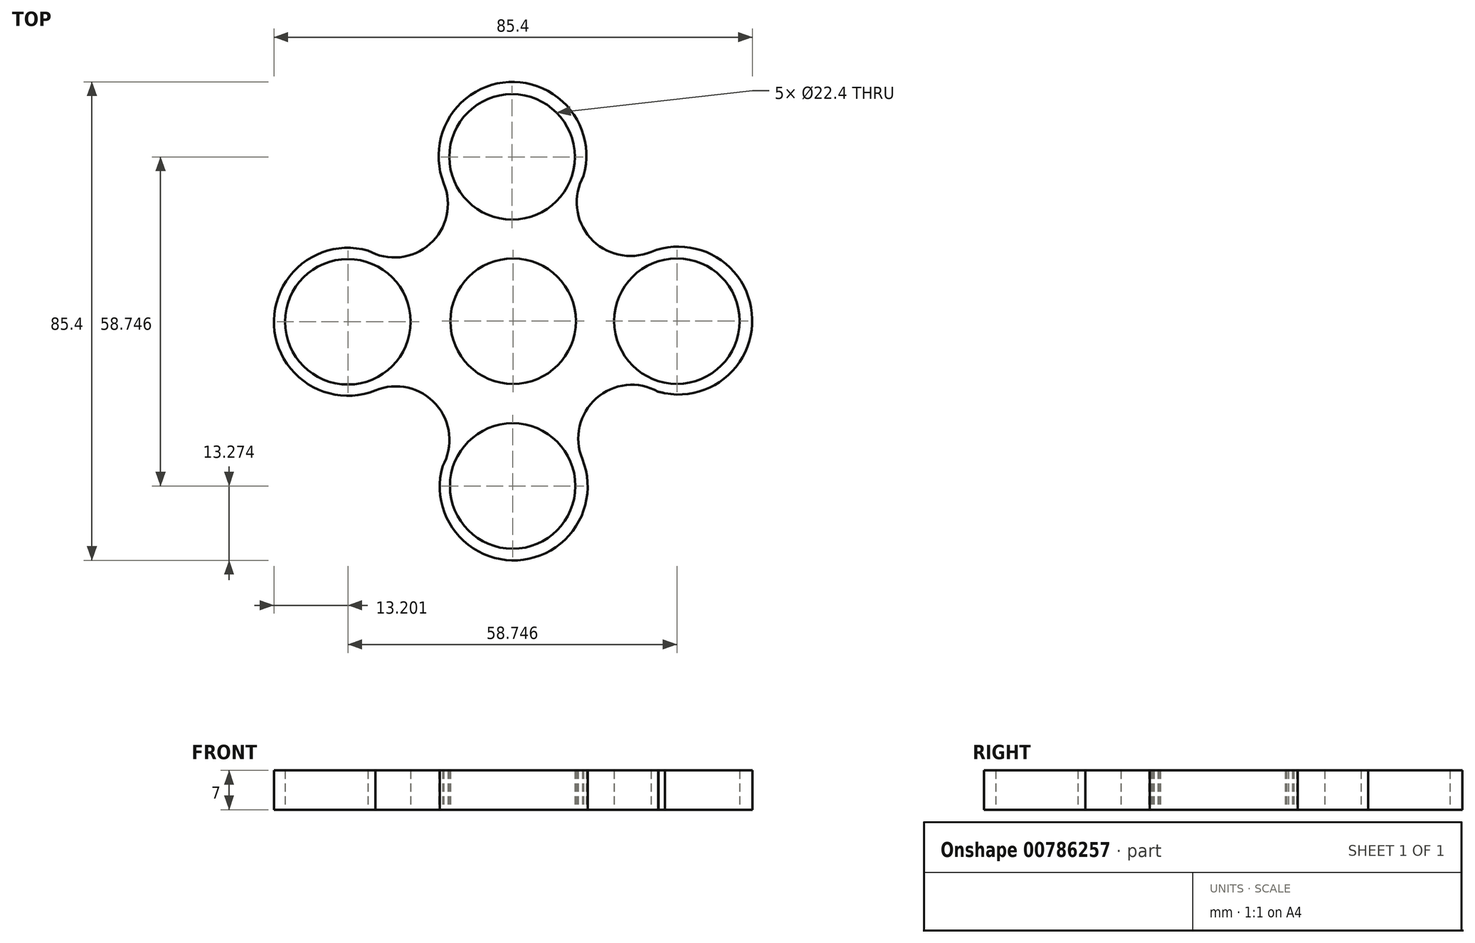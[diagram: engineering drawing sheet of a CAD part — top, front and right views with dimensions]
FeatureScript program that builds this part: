
annotation { "Feature Type Name" : "Feature", "Feature Type Description" : "" }
export const myFeature = defineFeature(function(context is Context, id is Id, definition is map)
    precondition{}
    {
        {
            var Q0;
            Q0=qCreatedBy(makeId("Top.planeOp"),FACE);
            var sketch = newSketch(context, id + "F0", { "sketchPlane" : qUnion([Q0])});
            skCircle(sketch, "E0", {"center": v(0, 0) * mm, "radius": 11.2 * mm});
            skCircle(sketch, "E1", {"center": v(29.25, 0) * mm, "radius": 11.2 * mm});
            skCircle(sketch, "E2.1.0", {"center": v(-0.18, 29.32) * mm, "radius": 11.2 * mm});
            skCircle(sketch, "E2.2.0", {"center": v(-29.5, -0.1) * mm, "radius": 11.2 * mm});
            skArc(sketch, "E2.2.1", {"start": v(-25.9, 12.6) * mm, "mid": v(-26.73, 12.8) * mm, "end": v(-27.57, 12.95) * mm});
            skCircle(sketch, "E2.3.0", {"center": v(-0.07, -29.43) * mm, "radius": 11.2 * mm});
            skArc(sketch, "E2.3.1", {"start": v(-12.77, -25.83) * mm, "mid": v(-12.96, -26.59) * mm, "end": v(-13.1, -27.36) * mm});
            skPoint(sketch, "E2.center", {"position": v(-0.13, -0.05) * mm});
            skArc(sketch, "E3.2.0", {"start": v(-13.1, -27.36) * mm, "mid": v(-12.91, -26.6) * mm, "end": v(-12.77, -25.83) * mm});
            skArc(sketch, "E3.3.0", {"start": v(27.2, -12.9) * mm, "mid": v(26.58, -12.74) * mm, "end": v(25.95, -12.6) * mm});
            skPoint(sketch, "E3.center", {"position": v(-0.18, 0.03) * mm});
            skArc(sketch, "E4", {"start": v(-25.9, 12.6) * mm, "mid": v(-42.68, -0.8) * mm, "end": v(-24.6, -12.37) * mm});
            skArc(sketch, "E5.1.0", {"start": v(-12.6, -25.9) * mm, "mid": v(0.8, -42.68) * mm, "end": v(12.37, -24.6) * mm});
            skArc(sketch, "E5.2.0", {"start": v(25.9, -12.6) * mm, "mid": v(42.68, 0.8) * mm, "end": v(24.6, 12.37) * mm});
            skArc(sketch, "E5.3.0", {"start": v(12.6, 25.9) * mm, "mid": v(-0.8, 42.68) * mm, "end": v(-12.37, 24.6) * mm});
            skPoint(sketch, "E6.orphan", {"position": v(24.24, 12.42) * mm});
            skArc(sketch, "E7", {"start": v(12.6, 25.9) * mm, "mid": v(13.77, 14.85) * mm, "end": v(24.6, 12.37) * mm});
            skArc(sketch, "E8.1.0", {"start": v(-25.9, 12.6) * mm, "mid": v(-14.85, 13.77) * mm, "end": v(-12.37, 24.6) * mm});
            skArc(sketch, "E8.2.0", {"start": v(-12.6, -25.9) * mm, "mid": v(-13.77, -14.85) * mm, "end": v(-24.6, -12.37) * mm});
            skArc(sketch, "E8.3.0", {"start": v(25.9, -12.6) * mm, "mid": v(14.85, -13.77) * mm, "end": v(12.37, -24.6) * mm});
            skArc(sketch, "E9.trimOffspring", {"start": v(12.2, -24.19) * mm, "mid": v(12.2, -24.3) * mm, "end": v(12.2, -24.4) * mm});
            skSolve(sketch);
        }
        {
            var Q0;
            Q0=makeQuery(id+"F0.imprint","IMPRINT",FACE,{"disambiguationData":[TD([[makeQuery(id+"F0.imprint","IMPRINT",EDGE,{"derivedFrom":sQuery(id+"F0.wireOp",EDGE,"E0")}),-1.0]])]});
            extrude(context, id + "F1", {"entities" : qUnion([Q0]), "depth" : 7 * mm, "offsetDistance" : 25 * mm});
        }
    });
